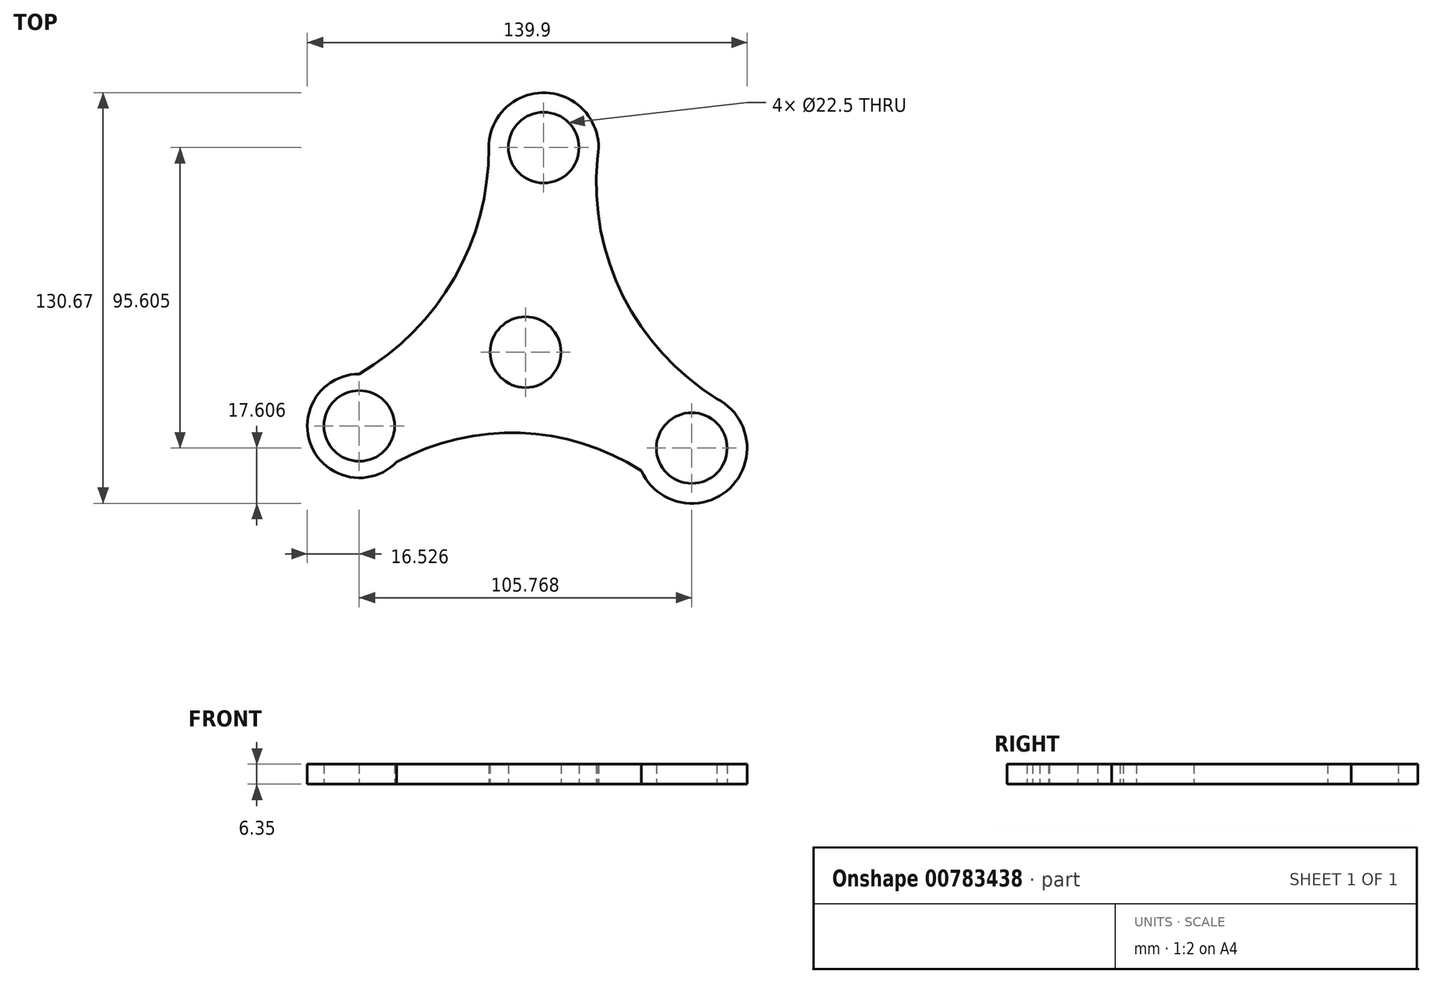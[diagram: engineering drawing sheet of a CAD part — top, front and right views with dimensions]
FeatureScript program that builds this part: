
annotation { "Feature Type Name" : "Feature", "Feature Type Description" : "" }
export const myFeature = defineFeature(function(context is Context, id is Id, definition is map)
    precondition{}
    {
        {
            var Q0;
            Q0=qCreatedBy(makeId("Top.planeOp"),FACE);
            var sketch = newSketch(context, id + "F0", { "sketchPlane" : qUnion([Q0])});
            skCircle(sketch, "E0.0", {"center": v(5.77, 65.1) * mm, "radius": 11.25 * mm});
            skCircle(sketch, "E1", {"center": v(0, 0) * mm, "radius": 11.25 * mm});
            skCircle(sketch, "E2.1.0", {"center": v(-52.9, -23.47) * mm, "radius": 11.25 * mm});
            skCircle(sketch, "E2.2.0", {"center": v(52.87, -30.51) * mm, "radius": 11.25 * mm});
            skArc(sketch, "E3.0", {"start": v(-52.9, -6.94) * mm, "mid": v(-68.1, -29.94) * mm, "end": v(-40.98, -34.92) * mm});
            skArc(sketch, "E4.0", {"start": v(36.83, -37.75) * mm, "mid": v(65, -43.27) * mm, "end": v(60.9, -14.85) * mm});
            skArc(sketch, "E5.0", {"start": v(22.8, 61.3) * mm, "mid": v(7.68, 82.44) * mm, "end": v(-11.7, 65.1) * mm});
            skArc(sketch, "E6", {"start": v(-52.9, -6.94) * mm, "mid": v(-22.65, 23.56) * mm, "end": v(-11.7, 65.1) * mm});
            skArc(sketch, "E7.1.0", {"start": v(36.83, -37.75) * mm, "mid": v(-1.69, -25.7) * mm, "end": v(-40.98, -34.92) * mm});
            skArc(sketch, "E7.2.0", {"start": v(22.8, 61.3) * mm, "mid": v(31.04, 17.81) * mm, "end": v(60.9, -14.85) * mm});
            skSolve(sketch);
        }
        {
            var Q0;
            Q0=makeQuery(id+"F0.imprint","IMPRINT",FACE,{"disambiguationData":[TD([[makeQuery(id+"F0.imprint","IMPRINT",EDGE,{"derivedFrom":sQuery(id+"F0.wireOp",EDGE,"0b945fb4-2562-4920-867a-45dda54a84b5.1.0")}),-1.0]])]});
            var sketch = newSketch(context, id + "F1", { "sketchPlane" : qUnion([Q0])});
            skSolve(sketch);
        }
        {
            var Q0;
            Q0=makeQuery(id+"F0.imprint","IMPRINT",FACE,{"disambiguationData":[TD([[makeQuery(id+"F0.imprint","IMPRINT",EDGE,{"derivedFrom":sQuery(id+"F0.wireOp",EDGE,"E0.0")}),-1.0]])]});
            extrude(context, id + "F2", {"entities" : qUnion([Q0]), "depth" : 6.35 * mm, "offsetDistance" : 25.4 * mm});
        }
        {
            var Q0;
            Q0 = qSketchRegion(id + "F0", true);
            extrude(context, id + "F3", {"entities" : qUnion([Q0]), "operationType" : NewBodyOperationType.ADD, "depth" : 6.35 * mm, "offsetDistance" : 25.4 * mm});
        }
    });
